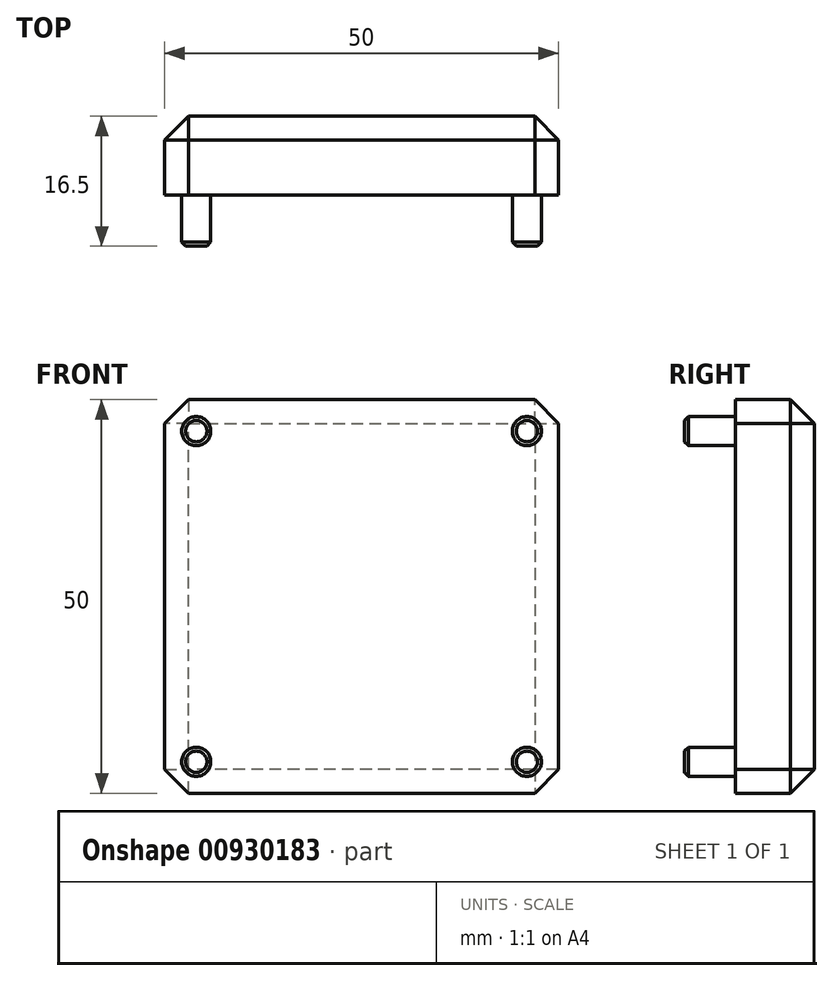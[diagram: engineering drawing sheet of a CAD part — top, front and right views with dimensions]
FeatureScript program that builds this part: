
annotation { "Feature Type Name" : "Feature", "Feature Type Description" : "" }
export const myFeature = defineFeature(function(context is Context, id is Id, definition is map)
    precondition{}
    {
        {
            var Q0;
            Q0=qCreatedBy(makeId("Front.planeOp"),FACE);
            var sketch = newSketch(context, id + "F0", { "sketchPlane" : qUnion([Q0])});
            skLineSegment(sketch, "E0.bottom", {"start": v(0, 0) * mm, "end": v(50, 0) * mm});
            skLineSegment(sketch, "E0.top", {"start": v(0, 50) * mm, "end": v(50, 50) * mm});
            skLineSegment(sketch, "E0.left", {"start": v(0, 0) * mm, "end": v(0, 50) * mm});
            skLineSegment(sketch, "E0.right", {"start": v(50, 0) * mm, "end": v(50, 50) * mm});
            skSolve(sketch);
        }
        {
            var Q0;
            Q0=makeQuery(id+"F0.imprint","IMPRINT",FACE,{"disambiguationData":[TD([[makeQuery(id+"F0.imprint","IMPRINT",EDGE,{"derivedFrom":sQuery(id+"F0.wireOp",EDGE,"E0.bottom")}),1.0]])]});
            extrude(context, id + "F1", {"entities" : qUnion([Q0]), "depth" : 10 * mm, "offsetDistance" : 25 * mm});
        }
        {
            var Q0;
            Q0=makeQuery(id+"F1.opExtrude","CAP_FACE",FACE,{"disambiguationData":[OSD([sQuery(id+"F0.wireOp",EDGE,"E0.bottom"),sQuery(id+"F0.wireOp",EDGE,"E0.top"),sQuery(id+"F0.wireOp",EDGE,"E0.left"),sQuery(id+"F0.wireOp",EDGE,"E0.right")])],"isStart":false});
            var sketch = newSketch(context, id + "F2", { "sketchPlane" : qUnion([Q0])});
            skCircle(sketch, "E1", {"center": v(4, 46) * mm, "radius": 1.85 * mm});
            skCircle(sketch, "E2", {"center": v(46, 46) * mm, "radius": 1.85 * mm});
            skCircle(sketch, "E3", {"center": v(46, 4) * mm, "radius": 1.85 * mm});
            skCircle(sketch, "E4", {"center": v(4, 4) * mm, "radius": 1.85 * mm});
            skSolve(sketch);
        }
        {
            var Q0;
            Q0 = qSketchRegion(id + "F2", true);
            extrude(context, id + "F3", {"entities" : qUnion([Q0]), "operationType" : NewBodyOperationType.ADD, "depth" : 6.5 * mm, "offsetDistance" : 25 * mm});
        }
        {
            var Q0;
            Q0=makeQuery(id+"F3.opExtrude","CAP_EDGE",EDGE,{"disambiguationData":[OSD([sQuery(id+"F2.wireOp",EDGE,"E4")])],"isStart":false});
            var Q1;
            Q1=makeQuery(id+"F3.opExtrude","CAP_EDGE",EDGE,{"disambiguationData":[OSD([sQuery(id+"F2.wireOp",EDGE,"E3")])],"isStart":false});
            var Q2;
            Q2=makeQuery(id+"F3.opExtrude","CAP_EDGE",EDGE,{"disambiguationData":[OSD([sQuery(id+"F2.wireOp",EDGE,"E2")])],"isStart":false});
            var Q3;
            Q3=makeQuery(id+"F3.opExtrude","CAP_EDGE",EDGE,{"disambiguationData":[OSD([sQuery(id+"F2.wireOp",EDGE,"E1")])],"isStart":false});
            chamfer(context, id + "F4", {"entities" : qUnion([Q0, Q1, Q2, Q3]), "width" : .5 * mm, "tangentPropagation" : true});
        }
        {
            var Q0;
            Q0=makeQuery(id+"F1.opExtrude","SWEPT_EDGE",EDGE,{"disambiguationData":[OSD([sQuery(id+"F0.wireOp",EDGE,"E0.top"),sQuery(id+"F0.wireOp",EDGE,"E0.left")])]});
            var Q1;
            Q1=makeQuery(id+"F1.opExtrude","SWEPT_EDGE",EDGE,{"disambiguationData":[OSD([sQuery(id+"F0.wireOp",EDGE,"E0.top"),sQuery(id+"F0.wireOp",EDGE,"E0.right")])]});
            var Q2;
            Q2=makeQuery(id+"F1.opExtrude","SWEPT_EDGE",EDGE,{"disambiguationData":[OSD([sQuery(id+"F0.wireOp",EDGE,"E0.bottom"),sQuery(id+"F0.wireOp",EDGE,"E0.right")])]});
            var Q3;
            Q3=makeQuery(id+"F1.opExtrude","SWEPT_EDGE",EDGE,{"disambiguationData":[OSD([sQuery(id+"F0.wireOp",EDGE,"E0.bottom"),sQuery(id+"F0.wireOp",EDGE,"E0.left")])]});
            var Q4;
            Q4=makeQuery(id+"F1.opExtrude","CAP_FACE",FACE,{"disambiguationData":[OSD([sQuery(id+"F0.wireOp",EDGE,"E0.bottom"),sQuery(id+"F0.wireOp",EDGE,"E0.top"),sQuery(id+"F0.wireOp",EDGE,"E0.left"),sQuery(id+"F0.wireOp",EDGE,"E0.right")])],"isStart":true});
            chamfer(context, id + "F5", {"entities" : qUnion([Q0, Q1, Q2, Q3, Q4]), "width" : 3 * mm, "tangentPropagation" : true});
        }
    });
